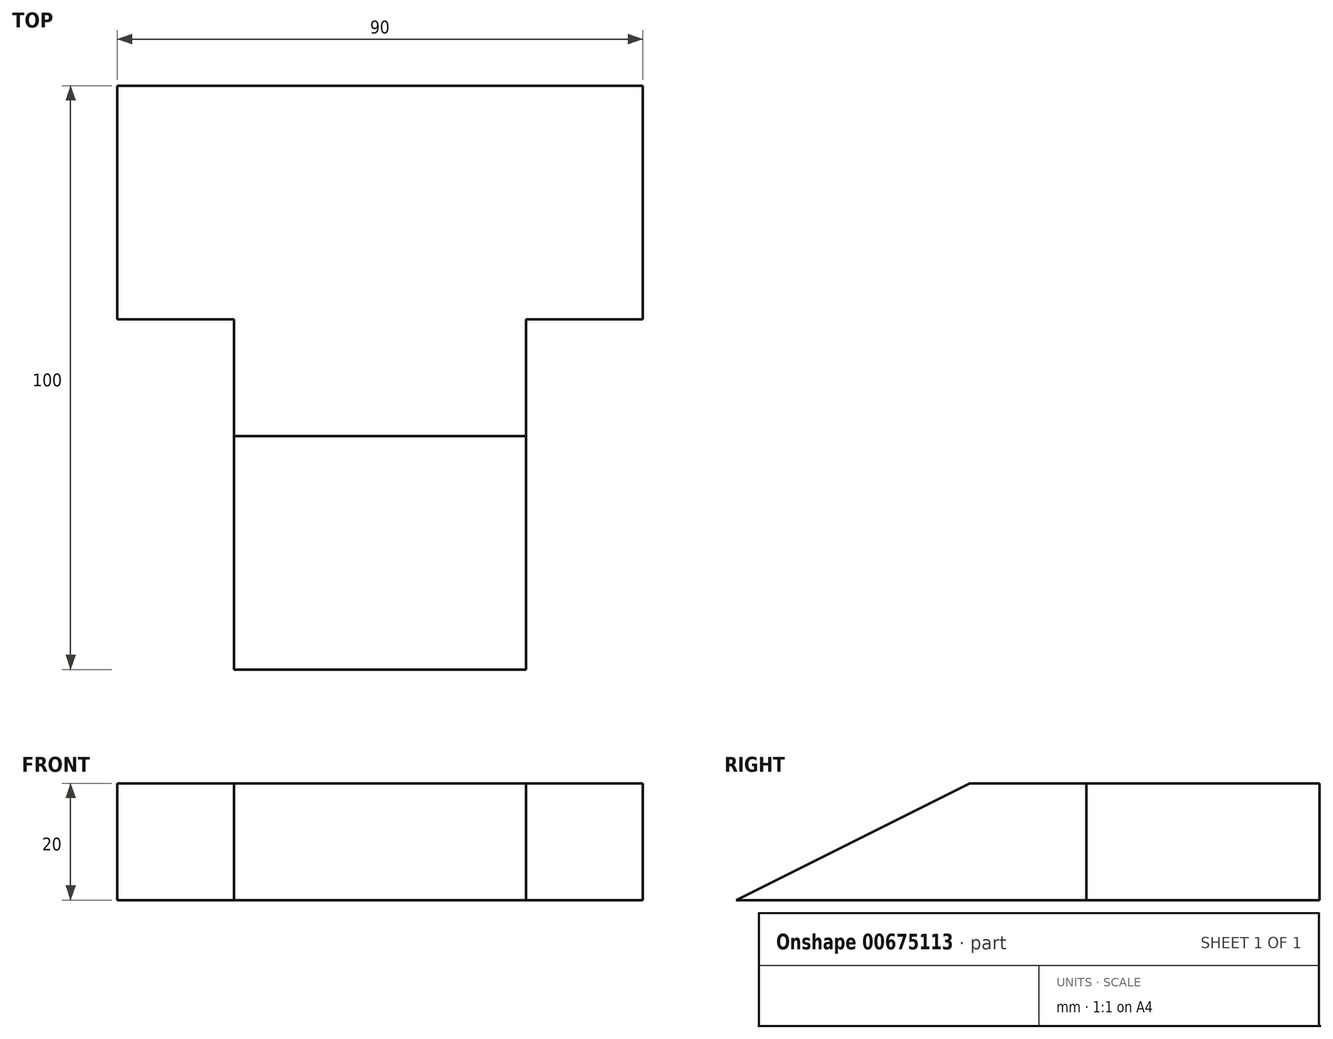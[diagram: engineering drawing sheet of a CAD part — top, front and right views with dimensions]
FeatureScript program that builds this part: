
annotation { "Feature Type Name" : "Feature", "Feature Type Description" : "" }
export const myFeature = defineFeature(function(context is Context, id is Id, definition is map)
    precondition{}
    {
        {
            var Q0;
            Q0=qCreatedBy(makeId("Front.planeOp"),FACE);
            var sketch = newSketch(context, id + "F0", { "sketchPlane" : qUnion([Q0])});
            skLineSegment(sketch, "E0.bottom", {"start": v(25, -10) * mm, "end": v(-25, -10) * mm});
            skLineSegment(sketch, "E0.top", {"start": v(25, 10) * mm, "end": v(-25, 10) * mm});
            skLineSegment(sketch, "E0.left", {"start": v(25, -10) * mm, "end": v(25, 10) * mm});
            skLineSegment(sketch, "E0.right", {"start": v(-25, -10) * mm, "end": v(-25, 10) * mm});
            skPoint(sketch, "E0.middle", {"position": v(0, 0) * mm});
            skSolve(sketch);
        }
        {
            var Q0;
            Q0 = qSketchRegion(id + "F0", true);
            extrude(context, id + "F1", {"entities" : qUnion([Q0]), "depth" : 100 * mm, "offsetDistance" : 25 * mm});
        }
        {
            var Q0;
            Q0=makeQuery(id+"F1.opExtrude","CAP_EDGE",EDGE,{"disambiguationData":[OSD([sQuery(id+"F0.wireOp",EDGE,"E0.top")])],"isStart":false});
            chamfer(context, id + "F2", {"entities" : qUnion([Q0]), "chamferType" : ChamferType.TWO_OFFSETS, "width1" : 20 * mm, "oppositeDirection" : false, "width2" : 40 * mm, "tangentPropagation" : true});
        }
        {
            var Q0;
            Q0=makeQuery(id+"F1.opExtrude","SWEPT_FACE",FACE,{"disambiguationData":[OSD([sQuery(id+"F0.wireOp",EDGE,"E0.left")])]});
            var sketch = newSketch(context, id + "F3", { "sketchPlane" : qUnion([Q0])});
            skLineSegment(sketch, "E1.bottom", {"start": v(0, 10) * mm, "end": v(-40, 10) * mm});
            skLineSegment(sketch, "E1.top", {"start": v(0, -10) * mm, "end": v(-40, -10) * mm});
            skLineSegment(sketch, "E1.left", {"start": v(0, 10) * mm, "end": v(0, -10) * mm});
            skLineSegment(sketch, "E1.right", {"start": v(-40, 10) * mm, "end": v(-40, -10) * mm});
            skSolve(sketch);
        }
        {
            var Q0;
            Q0 = qSketchRegion(id + "F3", true);
            extrude(context, id + "F4", {"entities" : qUnion([Q0]), "operationType" : NewBodyOperationType.ADD, "depth" : 20 * mm, "offsetDistance" : 25 * mm});
        }
        {
            var Q0;
            Q0=makeQuery(id+"F1.opExtrude","SWEPT_FACE",FACE,{"disambiguationData":[OSD([sQuery(id+"F0.wireOp",EDGE,"E0.right")])]});
            var sketch = newSketch(context, id + "F5", { "sketchPlane" : qUnion([Q0])});
            skLineSegment(sketch, "E2.bottom", {"start": v(0, 10) * mm, "end": v(40, 10) * mm});
            skLineSegment(sketch, "E2.top", {"start": v(0, -10) * mm, "end": v(40, -10) * mm});
            skLineSegment(sketch, "E2.left", {"start": v(0, 10) * mm, "end": v(0, -10) * mm});
            skLineSegment(sketch, "E2.right", {"start": v(40, 10) * mm, "end": v(40, -10) * mm});
            skSolve(sketch);
        }
        {
            var Q0;
            Q0 = qSketchRegion(id + "F5", true);
            extrude(context, id + "F6", {"entities" : qUnion([Q0]), "operationType" : NewBodyOperationType.ADD, "depth" : 20 * mm, "offsetDistance" : 25 * mm});
        }
    });
